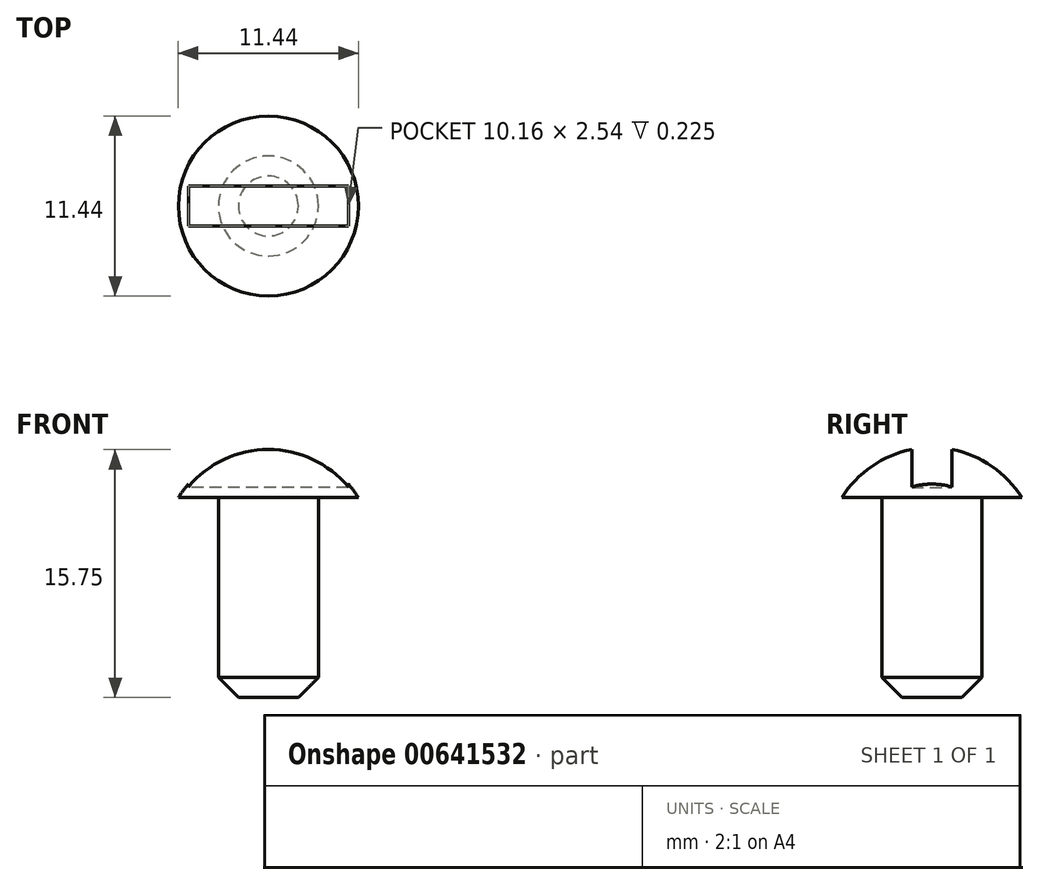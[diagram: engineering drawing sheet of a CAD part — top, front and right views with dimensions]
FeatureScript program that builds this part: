
annotation { "Feature Type Name" : "Feature", "Feature Type Description" : "" }
export const myFeature = defineFeature(function(context is Context, id is Id, definition is map)
    precondition{}
    {
        {
            var Q0;
            Q0=qCreatedBy(makeId("Front.planeOp"),FACE);
            var sketch = newSketch(context, id + "F0", { "sketchPlane" : qUnion([Q0])});
            skLineSegment(sketch, "E0", {"start": v(0, -12.7) * mm, "end": v(3.18, -12.7) * mm});
            skLineSegment(sketch, "E1", {"start": v(3.18, -12.7) * mm, "end": v(3.18, 0) * mm});
            skLineSegment(sketch, "E2", {"start": v(3.18, 0) * mm, "end": v(5.71, 0) * mm});
            skPoint(sketch, "E3", {"position": v(0, -3.56) * mm});
            skArc(sketch, "E4", {"start": v(5.71, 0) * mm, "mid": v(3.27, 2.33) * mm, "end": v(0, 3.18) * mm});
            skLineSegment(sketch, "E5", {"start": v(0, 3.17) * mm, "end": v(0, -12.7) * mm});
            skLineSegment(sketch, "E6", {"start": v(0, -12.7) * mm, "end": v(0, -20.57) * mm, "construction": true});
            skSolve(sketch);
        }
        {
            var Q0;
            Q0 = qSketchRegion(id + "F0", true);
            var Q1;
            Q1=sQuery(id+"F0.wireOp",EDGE,"E6");
            revolve(context, id + "F1", {"entities" : qUnion([Q0]), "axis" : qUnion([Q1]), "revolveType" : RevolveType.FULL});
        }
        {
            var Q0;
            Q0=qCreatedBy(makeId("Top.planeOp"),FACE);
            cPlane(context, id + "F2", {"entities" : qUnion([Q0]), "cplaneType" : CPlaneType.OFFSET, "offset" : 0.64 * mm, "width" : 152.4 * mm, "height" : 152.4 * mm});
        }
        {
            var Q0;
            Q0=qCreatedBy(id+"F2.planeOp",FACE);
            var sketch = newSketch(context, id + "F3", { "sketchPlane" : qUnion([Q0])});
            skLineSegment(sketch, "E7.bottom", {"start": v(5.08, -1.27) * mm, "end": v(-5.08, -1.27) * mm});
            skLineSegment(sketch, "E7.top", {"start": v(5.08, 1.27) * mm, "end": v(-5.08, 1.27) * mm});
            skLineSegment(sketch, "E7.left", {"start": v(5.08, -1.27) * mm, "end": v(5.08, 1.27) * mm});
            skLineSegment(sketch, "E7.right", {"start": v(-5.08, -1.27) * mm, "end": v(-5.08, 1.27) * mm});
            skPoint(sketch, "E7.middle", {"position": v(0, 0) * mm});
            skSolve(sketch);
        }
        {
            var Q0;
            Q0 = qSketchRegion(id + "F3", true);
            extrude(context, id + "F4", {"entities" : qUnion([Q0]), "operationType" : NewBodyOperationType.REMOVE, "endBound" : BoundingType.THROUGH_ALL, "depth" : 25.4 * mm, "offsetDistance" : 25.4 * mm});
        }
        {
            var Q0;
            Q0=makeQuery(id+"F1.opRevolve","SWEPT_EDGE",EDGE,{"disambiguationData":[OSD([sQuery(id+"F0.wireOp",EDGE,"E0"),sQuery(id+"F0.wireOp",EDGE,"E1")])]});
            chamfer(context, id + "F5", {"entities" : qUnion([Q0]), "width" : 1.27 * mm, "tangentPropagation" : true});
        }
    });
